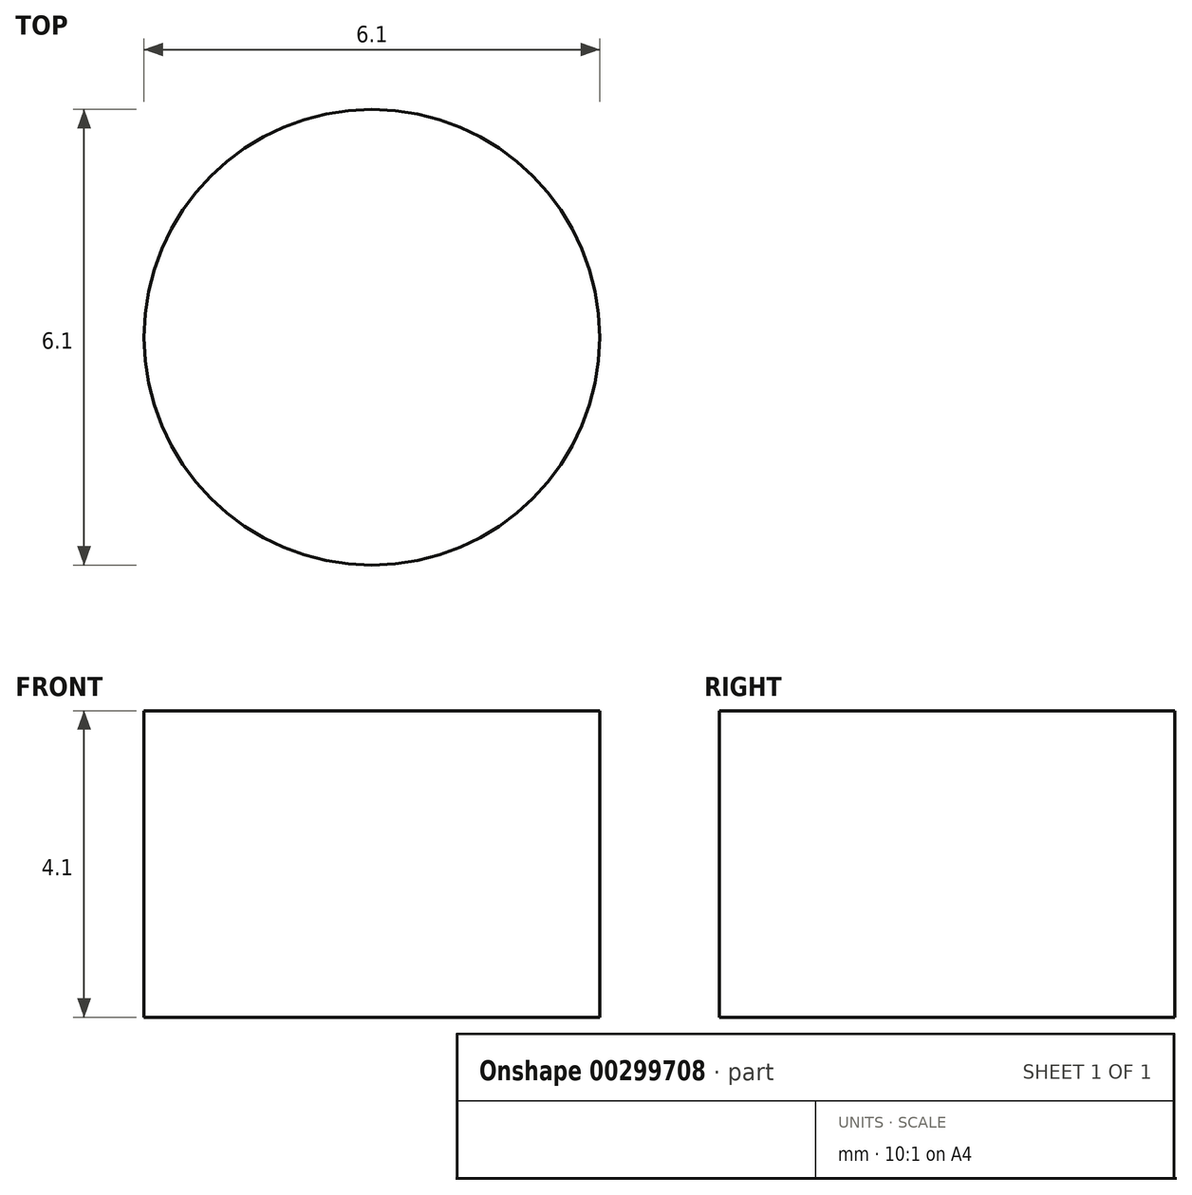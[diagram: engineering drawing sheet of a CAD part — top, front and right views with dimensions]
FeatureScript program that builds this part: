
annotation { "Feature Type Name" : "Feature", "Feature Type Description" : "" }
export const myFeature = defineFeature(function(context is Context, id is Id, definition is map)
    precondition{}
    {
        {
            var Q0;
            Q0=qCreatedBy(makeId("Top.planeOp"),FACE);
            var sketch = newSketch(context, id + "F0", { "sketchPlane" : qUnion([Q0])});
            skCircle(sketch, "E0", {"center": v(0, 0) * mm, "radius": 3.05 * mm});
            skSolve(sketch);
        }
        {
            var Q0;
            Q0=qSketchRegion(id+"F0",true);
            extrude(context, id + "F1", {"entities" : qUnion([Q0]), "depth" : 4.1 * mm});
        }
    });
